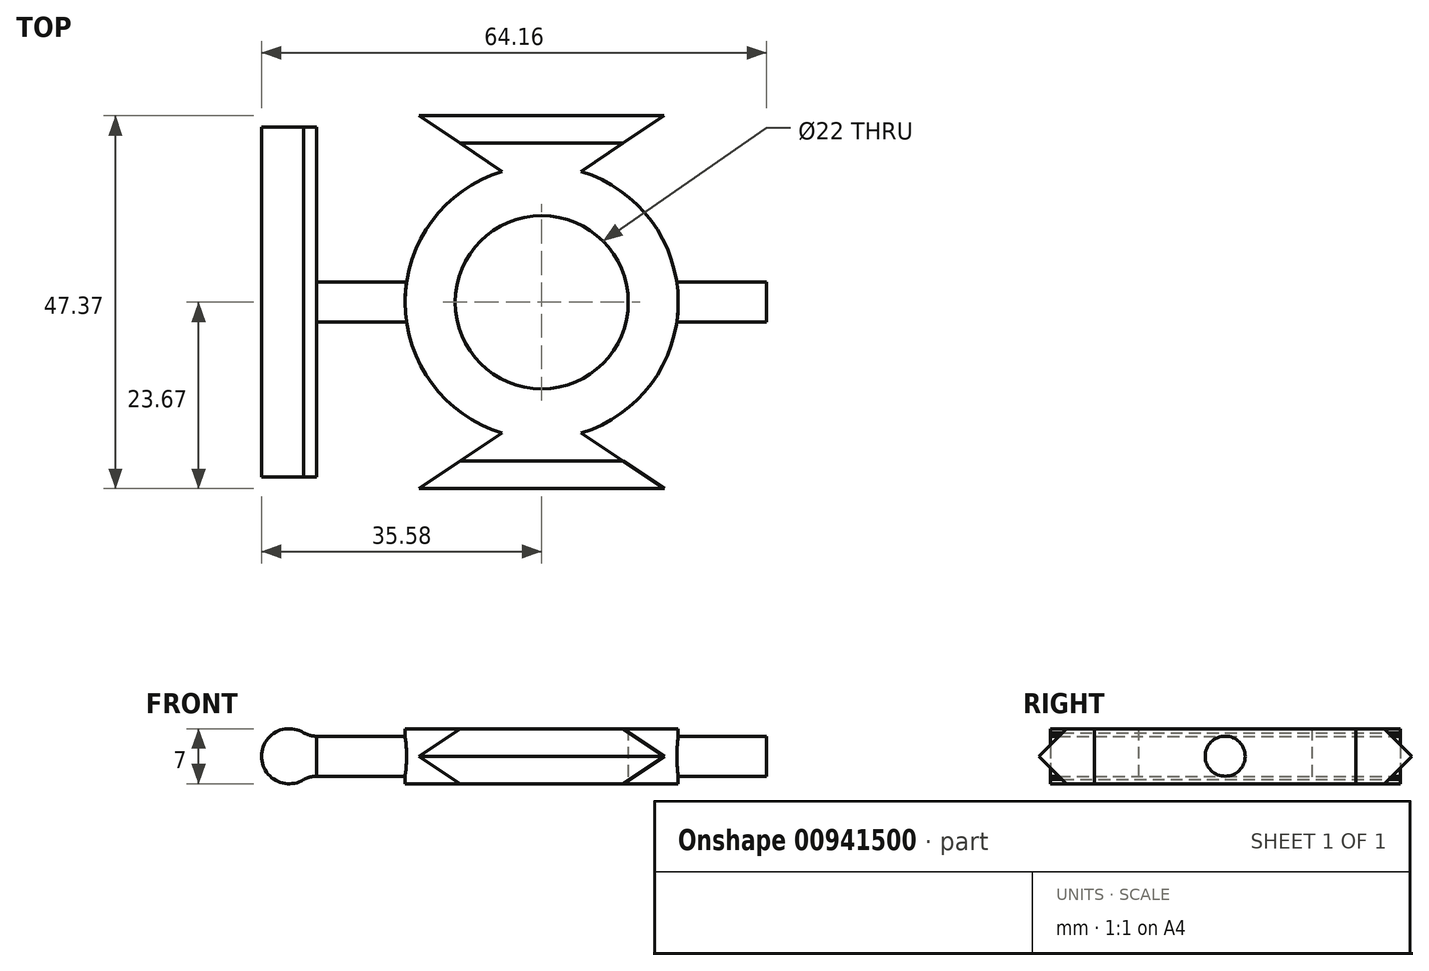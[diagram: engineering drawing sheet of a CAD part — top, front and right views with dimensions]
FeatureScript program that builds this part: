
annotation { "Feature Type Name" : "Feature", "Feature Type Description" : "" }
export const myFeature = defineFeature(function(context is Context, id is Id, definition is map)
    precondition{}
    {
        {
            var Q0;
            Q0=qCreatedBy(makeId("Top.planeOp"),FACE);
            var sketch = newSketch(context, id + "F0", { "sketchPlane" : qUnion([Q0])});
            skCircle(sketch, "E0", {"center": v(0, 0) * mm, "radius": 11 * mm});
            skCircle(sketch, "E1", {"center": v(0, 0) * mm, "radius": 17.35 * mm});
            skPoint(sketch, "E2", {"position": v(0, 17.35) * mm});
            skPoint(sketch, "E3", {"position": v(0, -17.35) * mm});
            skPoint(sketch, "E4", {"position": v(17.35, 0) * mm});
            skPoint(sketch, "E5", {"position": v(-17.35, 0) * mm});
            skLineSegment(sketch, "E6", {"start": v(5.03, 16.6) * mm, "end": v(15.56, 23.7) * mm});
            skLineSegment(sketch, "E7", {"start": v(15.56, 23.7) * mm, "end": v(-15.56, 23.7) * mm});
            skLineSegment(sketch, "E8", {"start": v(-15.56, 23.7) * mm, "end": v(-5.03, 16.6) * mm});
            skLineSegment(sketch, "E9", {"start": v(5.03, -16.6) * mm, "end": v(15.58, -23.67) * mm});
            skLineSegment(sketch, "E10", {"start": v(15.58, -23.67) * mm, "end": v(-15.58, -23.67) * mm});
            skLineSegment(sketch, "E11", {"start": v(-15.58, -23.67) * mm, "end": v(-5.03, -16.6) * mm});
            skSolve(sketch);
        }
        {
            var Q0;
            Q0 = qSketchRegion(id + "F0", true);
            extrude(context, id + "F1", {"entities" : qUnion([Q0]), "depth" : 7 * mm, "offsetDistance" : 25.4 * mm});
        }
        {
            var Q0;
            Q0=makeQuery(id+"F1.opExtrude","CAP_EDGE",EDGE,{"disambiguationData":[OSD([sQuery(id+"F0.wireOp",EDGE,"E7")])],"isStart":false});
            var Q1;
            Q1=makeQuery(id+"F1.opExtrude","CAP_EDGE",EDGE,{"disambiguationData":[OSD([sQuery(id+"F0.wireOp",EDGE,"E10")])],"isStart":false});
            var Q2;
            Q2=makeQuery(id+"F1.opExtrude","CAP_EDGE",EDGE,{"disambiguationData":[OSD([sQuery(id+"F0.wireOp",EDGE,"E10")])],"isStart":true});
            var Q3;
            Q3=makeQuery(id+"F1.opExtrude","CAP_EDGE",EDGE,{"disambiguationData":[OSD([sQuery(id+"F0.wireOp",EDGE,"E7")])],"isStart":true});
            chamfer(context, id + "F2", {"entities" : qUnion([Q0, Q1, Q2, Q3]), "width" : 3.5 * mm, "tangentPropagation" : true});
        }
        {
            var Q0;
            Q0=qCreatedBy(makeId("Right.planeOp"),FACE);
            var sketch = newSketch(context, id + "F3", { "sketchPlane" : qUnion([Q0])});
            skCircle(sketch, "E12", {"center": v(0, 3.5) * mm, "radius": 2.54 * mm});
            skSolve(sketch);
        }
        {
            var Q0;
            Q0 = qSketchRegion(id + "F3", true);
            extrude(context, id + "F4", {"entities" : qUnion([Q0]), "operationType" : NewBodyOperationType.ADD, "depth" : 57.15 * mm, "offsetDistance" : 25.4 * mm, "symmetric" : true});
        }
        {
            var Q0;
            Q0=qCreatedBy(makeId("Top.planeOp"),FACE);
            var sketch = newSketch(context, id + "F5", { "sketchPlane" : qUnion([Q0])});
            skCircle(sketch, "E13", {"center": v(0, 0) * mm, "radius": 11 * mm});
            skSolve(sketch);
        }
        {
            var Q0;
            Q0 = qSketchRegion(id + "F5", true);
            extrude(context, id + "F6", {"entities" : qUnion([Q0]), "operationType" : NewBodyOperationType.REMOVE, "depth" : 75.7 * mm, "offsetDistance" : 25.4 * mm});
        }
        {
            var Q0;
            Q0=qCreatedBy(makeId("Front.planeOp"),FACE);
            var sketch = newSketch(context, id + "F7", { "sketchPlane" : qUnion([Q0])});
            skCircle(sketch, "E14", {"center": v(-32.08, 3.5) * mm, "radius": 3.5 * mm});
            skLineSegment(sketch, "E15.0", {"start": v(-28.58, 6.04) * mm, "end": v(-28.58, 0.96) * mm});
            skLineSegment(sketch, "E16", {"start": v(-28.57, 6.04) * mm, "end": v(-17.35, 6.04) * mm});
            skArc(sketch, "E17", {"start": v(-30.22, 6.47) * mm, "mid": v(-29.42, 6.15) * mm, "end": v(-28.58, 6.04) * mm});
            skArc(sketch, "E18", {"start": v(-28.58, 0.96) * mm, "mid": v(-29.42, 0.85) * mm, "end": v(-30.22, 0.53) * mm});
            skSolve(sketch);
        }
        {
            var Q0;
            Q0 = qSketchRegion(id + "F7", true);
            extrude(context, id + "F8", {"entities" : qUnion([Q0]), "operationType" : NewBodyOperationType.ADD, "depth" : 44.45 * mm, "offsetDistance" : 25.4 * mm, "symmetric" : true});
        }
    });
